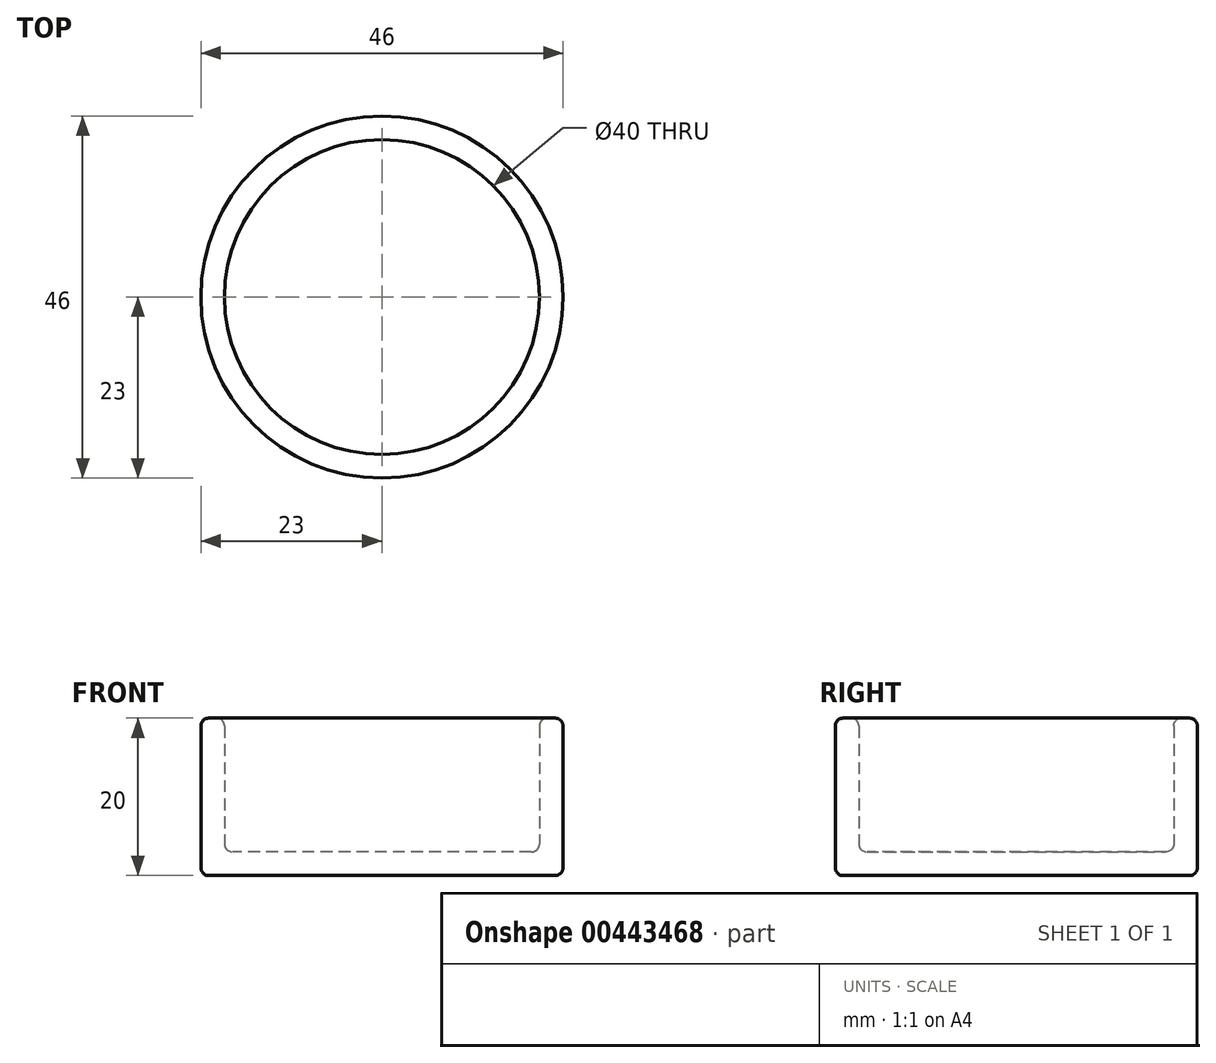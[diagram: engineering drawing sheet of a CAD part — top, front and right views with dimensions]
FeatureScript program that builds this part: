
annotation { "Feature Type Name" : "Feature", "Feature Type Description" : "" }
export const myFeature = defineFeature(function(context is Context, id is Id, definition is map)
    precondition{}
    {
        {
            var Q0;
            Q0=qCreatedBy(makeId("Top.planeOp"),FACE);
            var sketch = newSketch(context, id + "F0", { "sketchPlane" : qUnion([Q0])});
            skCircle(sketch, "E0", {"center": v(0, 0) * mm, "radius": 20 * mm});
            skCircle(sketch, "E1", {"center": v(0, 0) * mm, "radius": 23 * mm});
            skSolve(sketch);
        }
        {
            var Q0;
            Q0=makeQuery(id+"F0.imprint","IMPRINT",FACE,{"disambiguationData":[TD([[makeQuery(id+"F0.imprint","IMPRINT",EDGE,{"derivedFrom":sQuery(id+"F0.wireOp",EDGE,"E0")}),-1.0]])]});
            extrude(context, id + "F1", {"entities" : qUnion([Q0]), "depth" : 20 * mm});
        }
        {
            var Q0;
            Q0=qCreatedBy(makeId("Top.planeOp"),FACE);
            var sketch = newSketch(context, id + "F2", { "sketchPlane" : qUnion([Q0])});
            skCircle(sketch, "E2", {"center": v(0, 0) * mm, "radius": 23 * mm});
            skSolve(sketch);
        }
        {
            var Q0;
            Q0 = qSketchRegion(id + "F2", true);
            extrude(context, id + "F3", {"entities" : qUnion([Q0]), "operationType" : NewBodyOperationType.ADD, "depth" : 3 * mm});
        }
        {
            var Q0;
            Q0=makeQuery(id+"F3.opExtrude","CAP_FACE",FACE,{"disambiguationData":[OSD([sQuery(id+"F2.wireOp",EDGE,"E2")])],"isStart":false});
            var Q1;
            Q1=makeQuery(id+"F1.opExtrude","CAP_EDGE",EDGE,{"disambiguationData":[OSD([sQuery(id+"F0.wireOp",EDGE,"E0")])],"isStart":false});
            var Q2;
            Q2=makeQuery(id+"F1.opExtrude","CAP_EDGE",EDGE,{"disambiguationData":[OSD([sQuery(id+"F0.wireOp",EDGE,"E1")])],"isStart":false});
            var Q3;
            Q3=makeQuery(id+"F1.opExtrude","SWEPT_FACE",FACE,{"disambiguationData":[OSD([sQuery(id+"F0.wireOp",EDGE,"E1")])]});
            fillet(context, id + "F4", {"entities" : qUnion([Q0, Q1, Q2, Q3]), "radius" : 1 * mm, "tangentPropagation" : true, "allowEdgeOverflow" : false});
        }
    });
